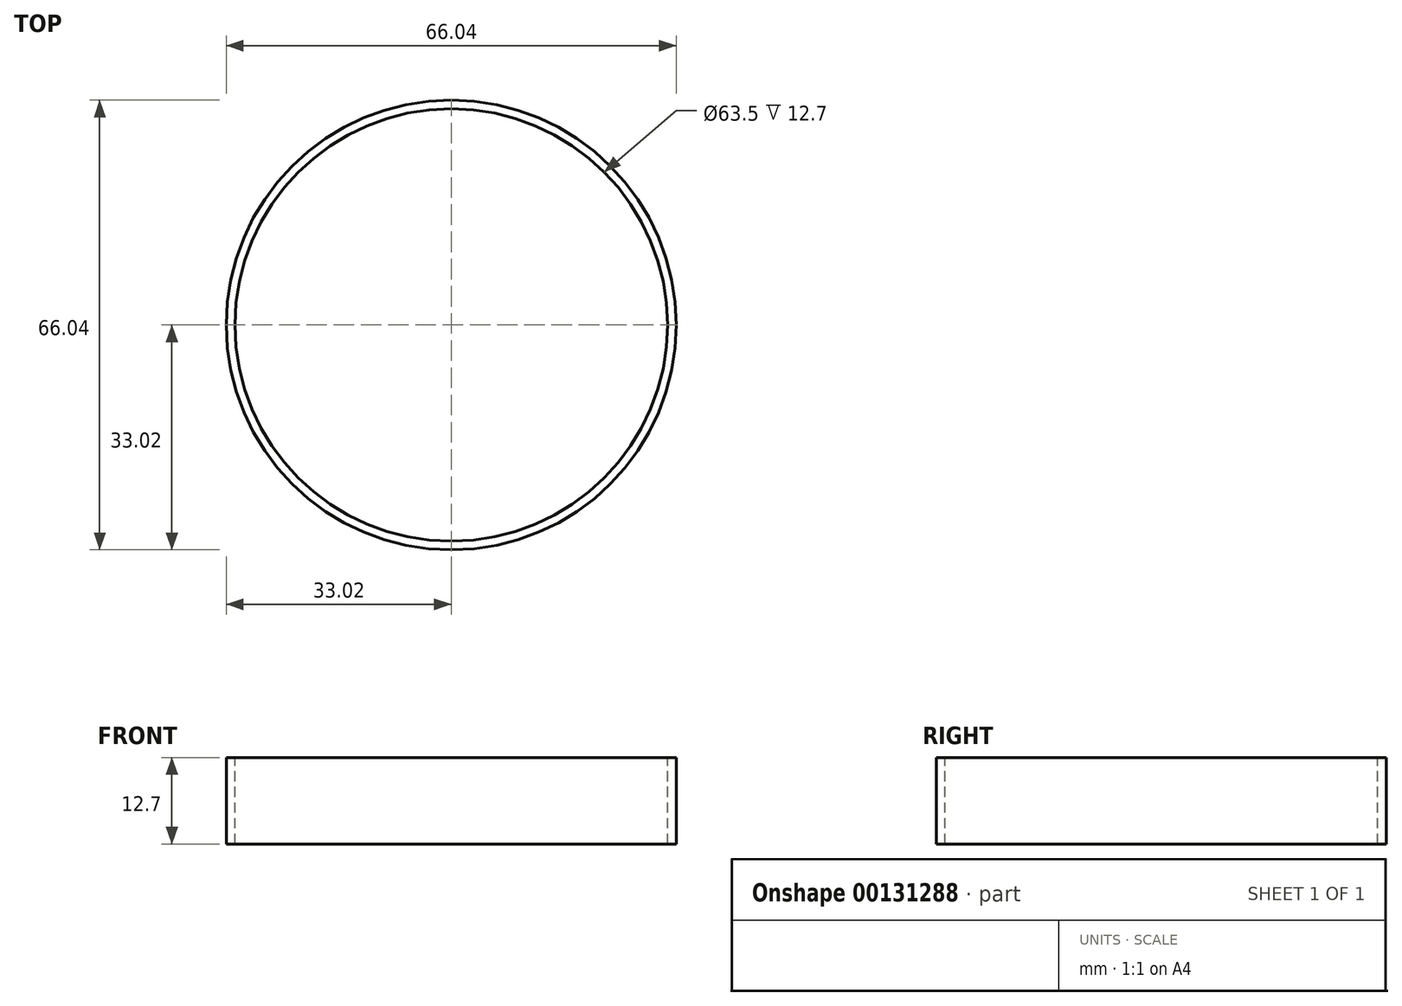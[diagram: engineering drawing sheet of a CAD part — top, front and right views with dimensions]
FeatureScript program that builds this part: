
annotation { "Feature Type Name" : "Feature", "Feature Type Description" : "" }
export const myFeature = defineFeature(function(context is Context, id is Id, definition is map)
    precondition{}
    {
        {
            var Q0;
            Q0=qCreatedBy(makeId("Front.planeOp"),FACE);
            var sketch = newSketch(context, id + "F0", { "sketchPlane" : qUnion([Q0])});
            skEllipticalArc(sketch, "E0", {});
            skFitSpline(sketch, "E1.0", {"points": [v(1.85, 77.7) * mm, v(0, 77.83) * mm, v(-1.85, 77.7) * mm, v(-4.29, 77.22) * mm, v(-7.25, 76.02) * mm, v(-10.64, 73.72) * mm, v(-13.85, 70.62) * mm, v(-16.88, 66.76) * mm, v(-19.74, 62.16) * mm, v(-21.96, 57.72) * mm, v(-23.64, 53.83) * mm, v(-24.85, 50.74) * mm, v(-26, 47.5) * mm, v(-27.43, 43) * mm, v(-29.06, 37.08) * mm, v(-30.73, 29.53) * mm, v(-32.12, 21.62) * mm, v(-33.22, 13.38) * mm, v(-33.88, 6.3) * mm, v(-34.26, 0.52) * mm, v(-34.46, -3.85) * mm, v(-34.56, -7.52) * mm, v(-34.6, -10.48) * mm, v(-34.61, -12.7) * mm, v(-34.6, -14.92) * mm, v(-34.56, -17.88) * mm, v(-34.46, -21.55) * mm, v(-34.26, -25.92) * mm, v(-33.88, -31.7) * mm, v(-33.22, -38.78) * mm, v(-32.12, -47.02) * mm, v(-30.73, -54.93) * mm, v(-29.06, -62.48) * mm, v(-27.43, -68.4) * mm, v(-26, -72.9) * mm, v(-24.85, -76.14) * mm, v(-23.64, -79.23) * mm, v(-21.96, -83.12) * mm, v(-19.74, -87.56) * mm, v(-16.88, -92.16) * mm, v(-13.85, -96.02) * mm, v(-10.64, -99.12) * mm, v(-7.25, -101.42) * mm, v(-4.29, -102.62) * mm, v(-1.85, -103.1) * mm, v(0, -103.23) * mm, v(1.85, -103.1) * mm, v(4.29, -102.62) * mm, v(7.25, -101.42) * mm, v(10.64, -99.12) * mm, v(13.85, -96.02) * mm, v(16.88, -92.16) * mm, v(19.74, -87.56) * mm, v(21.96, -83.12) * mm, v(23.64, -79.23) * mm, v(24.85, -76.14) * mm, v(26, -72.9) * mm, v(27.43, -68.4) * mm, v(29.06, -62.48) * mm, v(30.73, -54.93) * mm, v(32.12, -47.02) * mm, v(33.22, -38.78) * mm, v(33.88, -31.7) * mm, v(34.26, -25.92) * mm, v(34.46, -21.55) * mm, v(34.56, -17.88) * mm, v(34.6, -14.92) * mm, v(34.61, -12.7) * mm, v(34.6, -10.48) * mm, v(34.56, -7.52) * mm, v(34.46, -3.85) * mm, v(34.26, 0.52) * mm, v(33.88, 6.3) * mm, v(33.22, 13.38) * mm, v(32.12, 21.62) * mm, v(30.73, 29.53) * mm, v(29.06, 37.08) * mm, v(27.43, 43) * mm, v(26, 47.5) * mm, v(24.85, 50.74) * mm, v(23.64, 53.83) * mm, v(21.96, 57.72) * mm, v(19.74, 62.16) * mm, v(16.88, 66.76) * mm, v(13.85, 70.62) * mm, v(10.64, 73.72) * mm, v(7.25, 76.02) * mm, v(4.29, 77.22) * mm, v(1.85, 77.7) * mm, v(0, 77.83) * mm, v(-1.85, 77.7) * mm]});
            skLineSegment(sketch, "E2", {"start": v(-34.6, -12.7) * mm, "end": v(-33.02, -12.7) * mm});
            skLineSegment(sketch, "E3", {"start": v(33.02, -12.7) * mm, "end": v(34.6, -12.7) * mm});
            skLineSegment(sketch, "E4", {"start": v(0, 77.79) * mm, "end": v(0, -12.7) * mm});
            skPoint(sketch, "E5.orphan", {"position": v(0, 76.2) * mm});
            skLineSegment(sketch, "E6", {"start": v(0, -12.7) * mm, "end": v(0, -25.4) * mm});
            skLineSegment(sketch, "E7", {"start": v(31.75, -25.4) * mm, "end": v(31.75, -12.7) * mm});
            skLineSegment(sketch, "E8", {"start": v(31.75, -12.7) * mm, "end": v(33.02, -12.7) * mm});
            skLineSegment(sketch, "E9.bottom", {"start": v(31.75, -25.4) * mm, "end": v(33.02, -25.4) * mm});
            skLineSegment(sketch, "E9.right", {"start": v(33.02, -25.4) * mm, "end": v(33.02, -12.7) * mm});
            const initialGuessF0  = {"E0": [0, -0.0127, 0, 1, 0.0889, 0.03302, 4.71238898038469, 0]};
            skSetInitialGuess(sketch, initialGuessF0);
            skSolve(sketch);
        }
        {
            var Q0;
            {var subQ0=sQuery(id+"F0.wireOp",EDGE,"E0");Q0=makeQuery(id+"F0.imprint","IMPRINT",FACE,{"disambiguationData":[TD([[makeQuery(id+"F0.imprint","IMPRINT",EDGE,{"derivedFrom":subQ0}),-1.0]])]});}
            var Q1;
            Q1=makeQuery(id+"F0.imprint","IMPRINT",FACE,{"disambiguationData":[TD([[makeQuery(id+"F0.imprint","IMPRINT",EDGE,{"derivedFrom":sQuery(id+"F0.wireOp",EDGE,"E9.bottom")}),1.0]])]});
            var Q2;
            Q2=sQuery(id+"F0.wireOp",EDGE,"E4");
            revolve(context, id + "F1", {"entities" : qUnion([Q0, Q1]), "axis" : qUnion([Q2]), "revolveType" : RevolveType.FULL});
        }
    });
